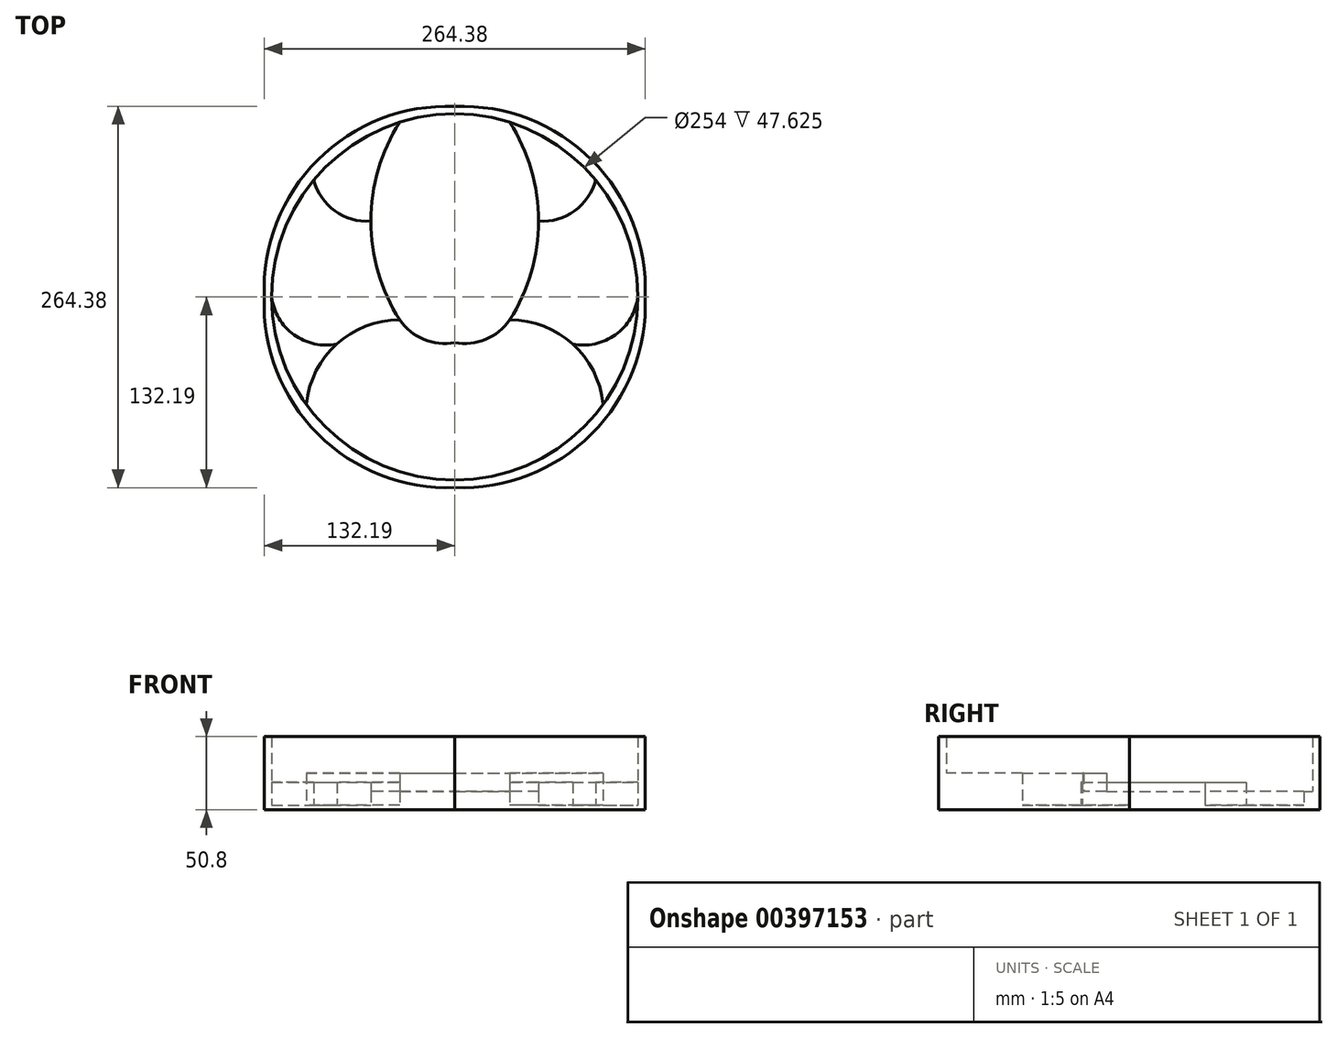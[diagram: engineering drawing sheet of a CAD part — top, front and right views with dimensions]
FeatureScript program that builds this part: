
annotation { "Feature Type Name" : "Feature", "Feature Type Description" : "" }
export const myFeature = defineFeature(function(context is Context, id is Id, definition is map)
    precondition{}
    {
        {
            var Q0;
            Q0=qCreatedBy(makeId("Top.planeOp"),FACE);
            var sketch = newSketch(context, id + "F0", { "sketchPlane" : qUnion([Q0])});
            skCircle(sketch, "E0", {"center": v(0, 0) * mm, "radius": 127 * mm});
            skArc(sketch, "E1", {"start": v(-38.1, -15.88) * mm, "mid": v(-21.39, -29.42) * mm, "end": v(0, -31.75) * mm});
            skArc(sketch, "E2", {"start": v(0, -31.75) * mm, "mid": v(21.39, -29.42) * mm, "end": v(38.1, -15.87) * mm});
            skArc(sketch, "E3", {"start": v(102.97, -74.34) * mm, "mid": v(81.76, -32.65) * mm, "end": v(38.1, -15.88) * mm});
            skArc(sketch, "E4", {"start": v(-38.1, -15.88) * mm, "mid": v(-81.76, -32.65) * mm, "end": v(-102.97, -74.34) * mm});
            skArc(sketch, "E5", {"start": v(81.76, -32.65) * mm, "mid": v(111.5, -26.17) * mm, "end": v(127, 0) * mm});
            skArc(sketch, "E6", {"start": v(-127, 0) * mm, "mid": v(-111.5, -26.17) * mm, "end": v(-81.76, -32.65) * mm});
            skArc(sketch, "E7", {"start": v(-38.1, 121.15) * mm, "mid": v(-58.17, 52.64) * mm, "end": v(-38.1, -15.88) * mm});
            skArc(sketch, "E8", {"start": v(38.1, -15.88) * mm, "mid": v(58.17, 52.64) * mm, "end": v(38.1, 121.15) * mm});
            skArc(sketch, "E9", {"start": v(-97.8, 81.03) * mm, "mid": v(-83.11, 59.67) * mm, "end": v(-58.17, 52.64) * mm});
            skArc(sketch, "E10", {"start": v(58.17, 52.64) * mm, "mid": v(83.11, 59.67) * mm, "end": v(97.8, 81.03) * mm});
            skLineSegment(sketch, "E11", {"start": v(0, -127) * mm, "end": v(0, -132.08) * mm});
            skLineSegment(sketch, "E12", {"start": v(-127, 0) * mm, "end": v(-132.08, 0) * mm});
            skLineSegment(sketch, "E13", {"start": v(127, 0) * mm, "end": v(132.08, 0) * mm});
            skLineSegment(sketch, "E14", {"start": v(0, 127) * mm, "end": v(0, 132.08) * mm});
            skArc(sketch, "E15", {"start": v(0, 132.08) * mm, "mid": v(-94.99, 94.99) * mm, "end": v(-132.08, 0) * mm});
            skArc(sketch, "E16", {"start": v(-132.08, 0) * mm, "mid": v(-94.99, -94.99) * mm, "end": v(0, -132.08) * mm});
            skArc(sketch, "E17", {"start": v(0, -132.08) * mm, "mid": v(94.99, -94.99) * mm, "end": v(132.08, 0) * mm});
            skArc(sketch, "E18", {"start": v(132.08, 0) * mm, "mid": v(94.99, 94.99) * mm, "end": v(0, 132.08) * mm});
            skLineSegment(sketch, "E19", {"start": v(0, -31.75) * mm, "end": v(0, -26.67) * mm});
            skLineSegment(sketch, "E20", {"start": v(-58.17, 52.64) * mm, "end": v(-53.09, 52.64) * mm});
            skLineSegment(sketch, "E21", {"start": v(0, 127) * mm, "end": v(0, 121.92) * mm});
            skLineSegment(sketch, "E22", {"start": v(58.17, 52.64) * mm, "end": v(53.09, 52.64) * mm});
            skSolve(sketch);
        }
        {
            var Q0;
            {var subQ0=sQuery(id+"F0.wireOp",EDGE,"E13");Q0=makeQuery(id+"F0.imprint","IMPRINT",FACE,{"disambiguationData":[TD([[makeQuery(id+"F0.imprint","IMPRINT",EDGE,{"derivedFrom":subQ0}),1.0]])]});}
            var Q1;
            {var subQ0=sQuery(id+"F0.wireOp",EDGE,"E12");Q1=makeQuery(id+"F0.imprint","IMPRINT",FACE,{"disambiguationData":[TD([[makeQuery(id+"F0.imprint","IMPRINT",EDGE,{"derivedFrom":subQ0}),-1.0]])]});}
            var Q2;
            {var subQ0=sQuery(id+"F0.wireOp",EDGE,"E11");Q2=makeQuery(id+"F0.imprint","IMPRINT",FACE,{"disambiguationData":[TD([[makeQuery(id+"F0.imprint","IMPRINT",EDGE,{"derivedFrom":subQ0}),1.0]])]});}
            var Q3;
            {var subQ1=sQuery(id+"F0.wireOp",EDGE,"E11");Q3=makeQuery(id+"F0.imprint","IMPRINT",FACE,{"disambiguationData":[TD([[makeQuery(id+"F0.imprint","IMPRINT",EDGE,{"derivedFrom":subQ1}),-1.0]])]});}
            extrude(context, id + "F1", {"entities" : qUnion([Q0, Q1, Q2, Q3]), "depth" : 50.8 * mm});
        }
        {
            var Q0;
            {var subQ1=sQuery(id+"F0.wireOp",EDGE,"E1");Q0=makeQuery(id+"F0.imprint","IMPRINT",FACE,{"disambiguationData":[TD([[makeQuery(id+"F0.imprint","IMPRINT",EDGE,{"derivedFrom":subQ1}),1.0]])]});}
            extrude(context, id + "F2", {"entities" : qUnion([Q0]), "operationType" : NewBodyOperationType.ADD, "depth" : 12.7 * mm});
        }
        {
            var Q0;
            {var subQ1=sQuery(id+"F0.wireOp",EDGE,"E1");Q0=makeQuery(id+"F0.imprint","IMPRINT",FACE,{"disambiguationData":[TD([[makeQuery(id+"F0.imprint","IMPRINT",EDGE,{"derivedFrom":subQ1}),-1.0]])]});}
            extrude(context, id + "F3", {"entities" : qUnion([Q0]), "operationType" : NewBodyOperationType.ADD, "depth" : 25.4 * mm});
        }
        {
            var Q0;
            {var subQ0=sQuery(id+"F0.wireOp",EDGE,"E6");Q0=makeQuery(id+"F0.imprint","IMPRINT",FACE,{"disambiguationData":[TD([[makeQuery(id+"F0.imprint","IMPRINT",EDGE,{"derivedFrom":subQ0}),1.0]])]});}
            var Q1;
            {var subQ0=sQuery(id+"F0.wireOp",EDGE,"E5");Q1=makeQuery(id+"F0.imprint","IMPRINT",FACE,{"disambiguationData":[TD([[makeQuery(id+"F0.imprint","IMPRINT",EDGE,{"derivedFrom":subQ0}),1.0]])]});}
            extrude(context, id + "F4", {"entities" : qUnion([Q0, Q1]), "operationType" : NewBodyOperationType.ADD, "depth" : 19.05 * mm});
        }
        {
            var Q0;
            {var subQ3=sQuery(id+"F0.wireOp",EDGE,"E10");Q0=makeQuery(id+"F0.imprint","IMPRINT",FACE,{"disambiguationData":[TD([[makeQuery(id+"F0.imprint","IMPRINT",EDGE,{"derivedFrom":subQ3}),1.0]])]});}
            var Q1;
            {var subQ3=sQuery(id+"F0.wireOp",EDGE,"E5");Q1=makeQuery(id+"F0.imprint","IMPRINT",FACE,{"disambiguationData":[TD([[makeQuery(id+"F0.imprint","IMPRINT",EDGE,{"derivedFrom":subQ3}),-1.0]])]});}
            var Q2;
            {var subQ3=sQuery(id+"F0.wireOp",EDGE,"E6");Q2=makeQuery(id+"F0.imprint","IMPRINT",FACE,{"disambiguationData":[TD([[makeQuery(id+"F0.imprint","IMPRINT",EDGE,{"derivedFrom":subQ3}),-1.0]])]});}
            var Q3;
            {var subQ3=sQuery(id+"F0.wireOp",EDGE,"E9");Q3=makeQuery(id+"F0.imprint","IMPRINT",FACE,{"disambiguationData":[TD([[makeQuery(id+"F0.imprint","IMPRINT",EDGE,{"derivedFrom":subQ3}),1.0]])]});}
            extrude(context, id + "F5", {"entities" : qUnion([Q0, Q1, Q2, Q3]), "operationType" : NewBodyOperationType.ADD, "depth" : 3.17 * mm});
        }
    });
